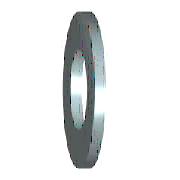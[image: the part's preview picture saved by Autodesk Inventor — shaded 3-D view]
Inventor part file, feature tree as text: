
AUTODESK INVENTOR PART (.ipt)
format: ipt  version: 2012 (Build 160160000, 160)  size: 95,232 bytes
history: native  units: mm (DEFAULTED — no unit token found)
features: other x1, plane x1
ambient origin geometry x7: Origin, YZ Plane, XY Plane, X Axis, Y Axis, Z Axis, Center Point
bodies: Solid1 (feature_tree), Body (feature_tree)
feature tree (2):
  other  "Work Axis1"
  plane  "Work Plane1"
